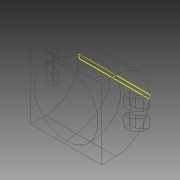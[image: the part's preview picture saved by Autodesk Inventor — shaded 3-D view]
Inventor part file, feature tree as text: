
AUTODESK INVENTOR PART (.ipt)
format: ipt  version: 2014 SP2 (Build 180246200, 246)  size: 217,088 bytes
history: native  units: mm
features: sketch x5, extrude x3, mirror x2, other x1, revolve x1, fillet x1, projected_geometry x1
ambient origin geometry x8: Origin, YZ Plane, XZ Plane, XY Plane, X Axis, Y Axis, Z Axis, Center Point
bodies: Solid1 (feature_tree)
feature tree (14):
  extrude  "Extrusion1"  Depth=53.0mm
  other  "Work Axis1"
  revolve  "Revolution1"  [1 undecoded]
  extrude  "Extrusion2"  TaperAngle=90.0deg  [1 undecoded]
  extrude  "Extrusion3"  Depth=4.0mm
  mirror  "Mirror1"
  mirror  "Mirror2"
  fillet  "Fillet1"  Radius=10.0mm
  sketch  "Sketch7"  dims[d11=5.0mm d12=0.0mm d14=15.0mm d18=45.0deg d19=4.0mm d20=0.0mm d21=0.0mm d22=25.0mm d23=1.0mm d24=1.0mm]
  sketch  "Sketch1"  dims[d0=53.0mm d1=53.0mm]
  sketch  "Sketch2"  dims[d2=36.0mm d3=0.0mm d5=33.0mm]
  sketch  "Sketch3"  dims[d6=24.0mm d7=90.0deg]
  sketch  "Sketch6"  dims[d8=8.0mm d9=4.0mm d10=10.0mm]
  projected_geometry  "Projected Loop3"
note: 2 required parameter values undecoded (feature->parameter linkage not recoverable at this tier; creation-order binding heuristic only, values carry confidence <= 0.55)